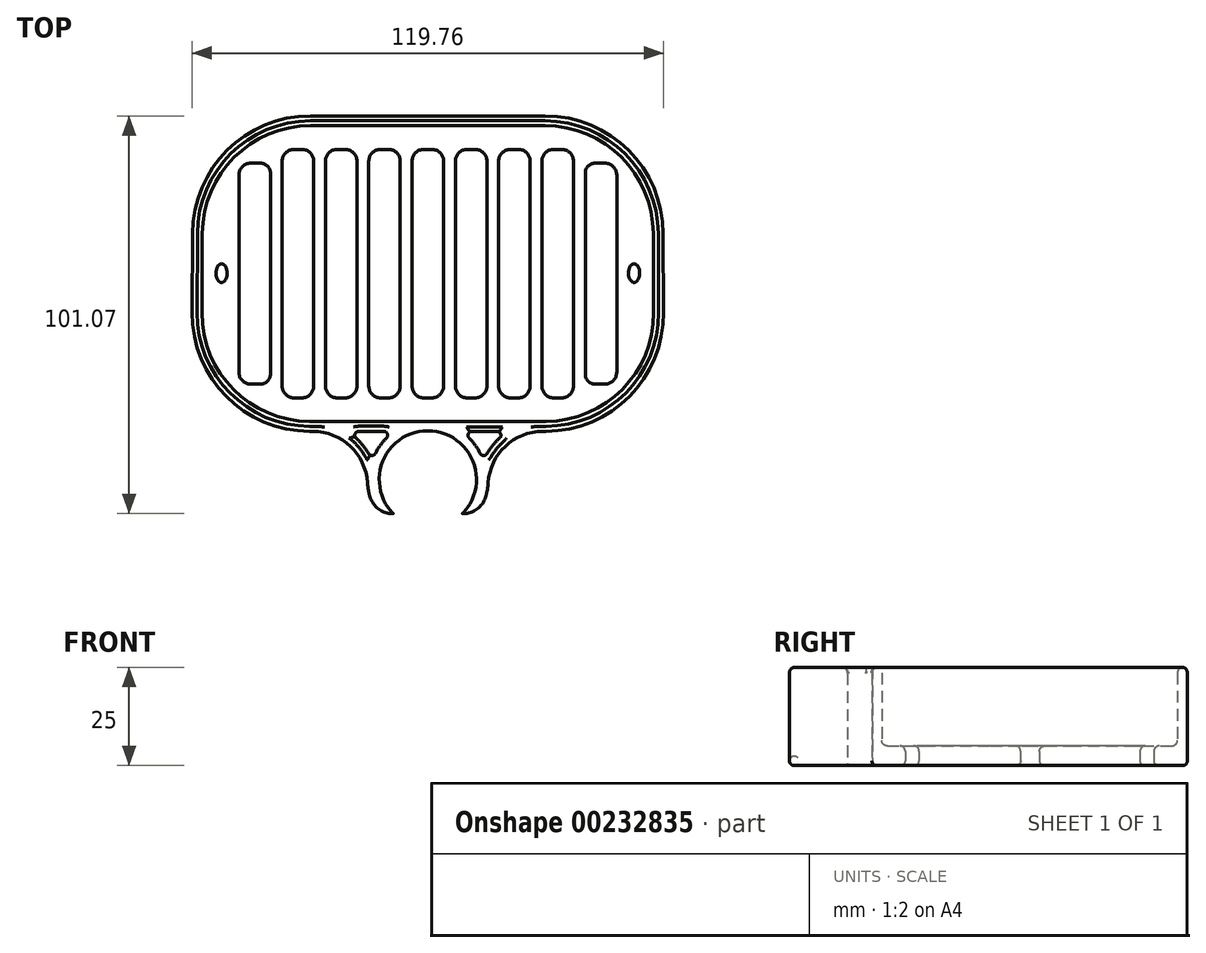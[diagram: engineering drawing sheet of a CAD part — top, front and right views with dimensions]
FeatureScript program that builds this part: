
annotation { "Feature Type Name" : "Feature", "Feature Type Description" : "" }
export const myFeature = defineFeature(function(context is Context, id is Id, definition is map)
    precondition{}
    {
        {
            var Q0;
            Q0=qCreatedBy(makeId("Top.planeOp"),FACE);
            var sketch = newSketch(context, id + "F0", { "sketchPlane" : qUnion([Q0])});
            skArc(sketch, "E0", {"start": v(8.75, -8.72) * mm, "mid": v(0, 12.35) * mm, "end": v(-8.75, -8.72) * mm});
            skLineSegment(sketch, "E1", {"start": v(8.95, -8.72) * mm, "end": v(8.75, -8.72) * mm});
            skArc(sketch, "E2.0", {"start": v(14.69, -4.46) * mm, "mid": v(15.1, -2.71) * mm, "end": v(15.32, -0.93) * mm});
            skLineSegment(sketch, "E3.trimOffspring", {"start": v(-8.75, -8.72) * mm, "end": v(-8.95, -8.72) * mm});
            skArc(sketch, "E4.trimOffspring", {"start": v(-15.32, -0.93) * mm, "mid": v(-15.1, -2.71) * mm, "end": v(-14.69, -4.46) * mm});
            skPoint(sketch, "E5.visualSharp", {"position": v(-12.64, -8.72) * mm});
            skArc(sketch, "E5.filletArc", {"start": v(-14.69, -4.46) * mm, "mid": v(-12.52, -7.53) * mm, "end": v(-8.95, -8.72) * mm});
            skPoint(sketch, "E6.visualSharp", {"position": v(12.64, -8.72) * mm});
            skArc(sketch, "E6.filletArc", {"start": v(8.95, -8.72) * mm, "mid": v(12.52, -7.53) * mm, "end": v(14.69, -4.46) * mm});
            skLineSegment(sketch, "E7", {"start": v(-30, 12.23) * mm, "end": v(-29.24, 12.22) * mm});
            skPoint(sketch, "E7.startSnap0", {"position": v(0, 12.35) * mm});
            skLineSegment(sketch, "E8", {"start": v(-59.88, 42.35) * mm, "end": v(-59.8, 62.47) * mm});
            skLineSegment(sketch, "E9", {"start": v(-29.8, 92.35) * mm, "end": v(0, 92.35) * mm});
            skLineSegment(sketch, "E10.MirrorCS", {"start": v(29.8, 92.35) * mm, "end": v(0, 92.35) * mm});
            skLineSegment(sketch, "E11.MirrorCS", {"start": v(59.88, 42.35) * mm, "end": v(59.8, 62.47) * mm});
            skLineSegment(sketch, "E12.MirrorCS", {"start": v(30, 12.23) * mm, "end": v(29.24, 12.22) * mm});
            skArc(sketch, "E13.filletArc", {"start": v(29.24, 12.22) * mm, "mid": v(19.68, 8.4) * mm, "end": v(15.32, -0.93) * mm});
            skArc(sketch, "E14.filletArc", {"start": v(-15.32, -0.93) * mm, "mid": v(-19.68, 8.4) * mm, "end": v(-29.24, 12.22) * mm});
            skPoint(sketch, "E15.visualSharp", {"position": v(-59.67, 92.35) * mm});
            skArc(sketch, "E15.filletArc", {"start": v(-29.8, 92.35) * mm, "mid": v(-50.96, 83.6) * mm, "end": v(-59.8, 62.47) * mm});
            skPoint(sketch, "E16.visualSharp", {"position": v(59.67, 92.35) * mm});
            skArc(sketch, "E16.filletArc", {"start": v(59.8, 62.47) * mm, "mid": v(50.96, 83.6) * mm, "end": v(29.8, 92.35) * mm});
            skPoint(sketch, "E17.visualSharp", {"position": v(60, 12.35) * mm});
            skArc(sketch, "E17.filletArc", {"start": v(30, 12.23) * mm, "mid": v(51.18, 21.1) * mm, "end": v(59.88, 42.35) * mm});
            skPoint(sketch, "E18.visualSharp", {"position": v(-60, 12.35) * mm});
            skArc(sketch, "E18.filletArc", {"start": v(-59.88, 42.35) * mm, "mid": v(-51.18, 21.1) * mm, "end": v(-30, 12.23) * mm});
            skLineSegment(sketch, "E19.0", {"start": v(29.99, 14.73) * mm, "end": v(25.24, 14.7) * mm});
            skArc(sketch, "E19.1", {"start": v(29.99, 14.73) * mm, "mid": v(49.4, 22.86) * mm, "end": v(57.38, 42.34) * mm});
            skLineSegment(sketch, "E19.2", {"start": v(57.38, 42.34) * mm, "end": v(57.3, 62.46) * mm});
            skArc(sketch, "E19.3", {"start": v(57.3, 62.46) * mm, "mid": v(49.2, 81.83) * mm, "end": v(29.8, 89.85) * mm});
            skLineSegment(sketch, "E19.4", {"start": v(29.8, 89.85) * mm, "end": v(0, 89.85) * mm});
            skLineSegment(sketch, "E19.5", {"start": v(-29.8, 89.85) * mm, "end": v(0, 89.85) * mm});
            skLineSegment(sketch, "E19.6", {"start": v(-29.99, 14.73) * mm, "end": v(-25.24, 14.7) * mm});
            skArc(sketch, "E19.7", {"start": v(-57.38, 42.34) * mm, "mid": v(-49.4, 22.86) * mm, "end": v(-29.99, 14.73) * mm});
            skLineSegment(sketch, "E19.8", {"start": v(-57.38, 42.34) * mm, "end": v(-57.3, 62.46) * mm});
            skArc(sketch, "E19.9", {"start": v(-29.8, 89.85) * mm, "mid": v(-49.2, 81.83) * mm, "end": v(-57.3, 62.46) * mm});
            skLineSegment(sketch, "E20", {"start": v(-25.24, 14.7) * mm, "end": v(25.24, 14.7) * mm});
            skLineSegment(sketch, "E21.bottom", {"start": v(-1, 83.85) * mm, "end": v(1, 83.85) * mm});
            skLineSegment(sketch, "E21.top", {"start": v(-1, 20.7) * mm, "end": v(1, 20.7) * mm});
            skLineSegment(sketch, "E21.left", {"start": v(-4, 80.85) * mm, "end": v(-4, 23.7) * mm});
            skLineSegment(sketch, "E21.right", {"start": v(4, 80.85) * mm, "end": v(4, 23.7) * mm});
            skPoint(sketch, "E22.visualSharp", {"position": v(-4, 83.85) * mm});
            skArc(sketch, "E22.filletArc", {"start": v(-1, 83.85) * mm, "mid": v(-3.12, 82.97) * mm, "end": v(-4, 80.85) * mm});
            skPoint(sketch, "E23.visualSharp", {"position": v(-4, 20.7) * mm});
            skArc(sketch, "E23.filletArc", {"start": v(-4, 23.7) * mm, "mid": v(-3.12, 21.59) * mm, "end": v(-1, 20.7) * mm});
            skPoint(sketch, "E24.visualSharp", {"position": v(4, 20.7) * mm});
            skArc(sketch, "E24.filletArc", {"start": v(1, 20.7) * mm, "mid": v(3.12, 21.59) * mm, "end": v(4, 23.7) * mm});
            skPoint(sketch, "E25.visualSharp", {"position": v(4, 83.85) * mm});
            skArc(sketch, "E25.filletArc", {"start": v(4, 80.85) * mm, "mid": v(3.12, 82.97) * mm, "end": v(1, 83.85) * mm});
            skPoint(sketch, "E26.1.0.0", {"position": v(7, 20.7) * mm});
            skLineSegment(sketch, "E26.1.0.1", {"start": v(7, 80.85) * mm, "end": v(7, 23.7) * mm});
            skPoint(sketch, "E26.1.0.2", {"position": v(7, 83.85) * mm});
            skPoint(sketch, "E26.1.0.3", {"position": v(15, 83.85) * mm});
            skPoint(sketch, "E26.1.0.4", {"position": v(15, 20.7) * mm});
            skLineSegment(sketch, "E26.1.0.5", {"start": v(15, 80.85) * mm, "end": v(15, 23.7) * mm});
            skArc(sketch, "E26.1.0.6", {"start": v(12, 20.7) * mm, "mid": v(14.12, 21.59) * mm, "end": v(15, 23.7) * mm});
            skArc(sketch, "E26.1.0.7", {"start": v(15, 80.85) * mm, "mid": v(14.12, 82.97) * mm, "end": v(12, 83.85) * mm});
            skArc(sketch, "E26.1.0.8", {"start": v(10, 83.85) * mm, "mid": v(7.88, 82.97) * mm, "end": v(7, 80.85) * mm});
            skLineSegment(sketch, "E26.1.0.9", {"start": v(10, 20.7) * mm, "end": v(12, 20.7) * mm});
            skArc(sketch, "E26.1.0.10", {"start": v(7, 23.7) * mm, "mid": v(7.88, 21.59) * mm, "end": v(10, 20.7) * mm});
            skLineSegment(sketch, "E26.1.0.11", {"start": v(10, 83.85) * mm, "end": v(12, 83.85) * mm});
            skPoint(sketch, "E26.2.0.0", {"position": v(18, 20.7) * mm});
            skLineSegment(sketch, "E26.2.0.1", {"start": v(18, 80.85) * mm, "end": v(18, 23.7) * mm});
            skPoint(sketch, "E26.2.0.2", {"position": v(18, 83.85) * mm});
            skPoint(sketch, "E26.2.0.3", {"position": v(26, 83.85) * mm});
            skPoint(sketch, "E26.2.0.4", {"position": v(26, 20.7) * mm});
            skLineSegment(sketch, "E26.2.0.5", {"start": v(26, 80.85) * mm, "end": v(26, 23.7) * mm});
            skArc(sketch, "E26.2.0.6", {"start": v(23, 20.7) * mm, "mid": v(25.12, 21.59) * mm, "end": v(26, 23.7) * mm});
            skArc(sketch, "E26.2.0.7", {"start": v(26, 80.85) * mm, "mid": v(25.12, 82.97) * mm, "end": v(23, 83.85) * mm});
            skArc(sketch, "E26.2.0.8", {"start": v(21, 83.85) * mm, "mid": v(18.88, 82.97) * mm, "end": v(18, 80.85) * mm});
            skLineSegment(sketch, "E26.2.0.9", {"start": v(21, 20.7) * mm, "end": v(23, 20.7) * mm});
            skArc(sketch, "E26.2.0.10", {"start": v(18, 23.7) * mm, "mid": v(18.88, 21.59) * mm, "end": v(21, 20.7) * mm});
            skLineSegment(sketch, "E26.2.0.11", {"start": v(21, 83.85) * mm, "end": v(23, 83.85) * mm});
            skPoint(sketch, "E26.3.0.0", {"position": v(29, 20.7) * mm});
            skLineSegment(sketch, "E26.3.0.1", {"start": v(29, 80.85) * mm, "end": v(29, 23.7) * mm});
            skPoint(sketch, "E26.3.0.2", {"position": v(29, 83.85) * mm});
            skPoint(sketch, "E26.3.0.3", {"position": v(37, 83.85) * mm});
            skPoint(sketch, "E26.3.0.4", {"position": v(37, 20.7) * mm});
            skLineSegment(sketch, "E26.3.0.5", {"start": v(37, 80.85) * mm, "end": v(37, 23.7) * mm});
            skArc(sketch, "E26.3.0.6", {"start": v(34, 20.7) * mm, "mid": v(36.12, 21.59) * mm, "end": v(37, 23.7) * mm});
            skArc(sketch, "E26.3.0.7", {"start": v(37, 80.85) * mm, "mid": v(36.12, 82.97) * mm, "end": v(34, 83.85) * mm});
            skArc(sketch, "E26.3.0.8", {"start": v(32, 83.85) * mm, "mid": v(29.88, 82.97) * mm, "end": v(29, 80.85) * mm});
            skLineSegment(sketch, "E26.3.0.9", {"start": v(32, 20.7) * mm, "end": v(34, 20.7) * mm});
            skArc(sketch, "E26.3.0.10", {"start": v(29, 23.7) * mm, "mid": v(29.88, 21.59) * mm, "end": v(32, 20.7) * mm});
            skLineSegment(sketch, "E26.3.0.11", {"start": v(32, 83.85) * mm, "end": v(34, 83.85) * mm});
            skPoint(sketch, "E26.4.0.0", {"position": v(40, 20.7) * mm});
            skLineSegment(sketch, "E26.4.0.1", {"start": v(40, 77.85) * mm, "end": v(40, 26.7) * mm});
            skPoint(sketch, "E26.4.0.2", {"position": v(40, 83.85) * mm});
            skPoint(sketch, "E26.4.0.3", {"position": v(48, 83.85) * mm});
            skPoint(sketch, "E26.4.0.4", {"position": v(48, 20.7) * mm});
            skLineSegment(sketch, "E26.4.0.5", {"start": v(48, 77.34) * mm, "end": v(48, 27.22) * mm});
            skLineSegment(sketch, "E26.direction1", {"start": v(-4, 20.7) * mm, "end": v(7, 20.7) * mm, "construction": true});
            skPoint(sketch, "E27.centerSnap0", {"position": v(4, 52.28) * mm});
            skEllipse(sketch, "E28", {"center": v(52.4, 52.4) * mm, "majorRadius": 2.38 * mm, "minorRadius": 1.43 * mm, "majorAxis": v(0, 1)});
            skPoint(sketch, "E28.centerSnap0", {"position": v(48, 52.4) * mm});
            skLineSegment(sketch, "E29.MirrorCS", {"start": v(-10, 20.7) * mm, "end": v(-12, 20.7) * mm});
            skArc(sketch, "E30.MirrorCS", {"start": v(-21, 83.85) * mm, "mid": v(-18.88, 82.97) * mm, "end": v(-18, 80.85) * mm});
            skLineSegment(sketch, "E31.MirrorCS", {"start": v(-10, 83.85) * mm, "end": v(-12, 83.85) * mm});
            skLineSegment(sketch, "E32.MirrorCS", {"start": v(-32, 83.85) * mm, "end": v(-34, 83.85) * mm});
            skLineSegment(sketch, "E33.MirrorCS", {"start": v(-32, 20.7) * mm, "end": v(-34, 20.7) * mm});
            skLineSegment(sketch, "E34.MirrorCS", {"start": v(-21, 20.7) * mm, "end": v(-23, 20.7) * mm});
            skArc(sketch, "E35.MirrorCS", {"start": v(-32, 83.85) * mm, "mid": v(-29.88, 82.97) * mm, "end": v(-29, 80.85) * mm});
            skArc(sketch, "E36.MirrorCS", {"start": v(-7, 23.7) * mm, "mid": v(-7.88, 21.59) * mm, "end": v(-10, 20.7) * mm});
            skArc(sketch, "E37.MirrorCS", {"start": v(-37, 80.85) * mm, "mid": v(-36.12, 82.97) * mm, "end": v(-34, 83.85) * mm});
            skArc(sketch, "E38.MirrorCS", {"start": v(-26, 80.85) * mm, "mid": v(-25.12, 82.97) * mm, "end": v(-23, 83.85) * mm});
            skLineSegment(sketch, "E39.MirrorCS", {"start": v(-21, 83.85) * mm, "end": v(-23, 83.85) * mm});
            skArc(sketch, "E40.MirrorCS", {"start": v(-15, 80.85) * mm, "mid": v(-14.12, 82.97) * mm, "end": v(-12, 83.85) * mm});
            skArc(sketch, "E41.MirrorCS", {"start": v(-18, 23.7) * mm, "mid": v(-18.88, 21.59) * mm, "end": v(-21, 20.7) * mm});
            skArc(sketch, "E42.MirrorCS", {"start": v(-10, 83.85) * mm, "mid": v(-7.88, 82.97) * mm, "end": v(-7, 80.85) * mm});
            skArc(sketch, "E43.MirrorCS", {"start": v(-23, 20.7) * mm, "mid": v(-25.12, 21.59) * mm, "end": v(-26, 23.7) * mm});
            skArc(sketch, "E44.MirrorCS", {"start": v(-29, 23.7) * mm, "mid": v(-29.88, 21.59) * mm, "end": v(-32, 20.7) * mm});
            skArc(sketch, "E45.MirrorCS", {"start": v(-12, 20.7) * mm, "mid": v(-14.12, 21.59) * mm, "end": v(-15, 23.7) * mm});
            skArc(sketch, "E46.MirrorCS", {"start": v(-34, 20.7) * mm, "mid": v(-36.12, 21.59) * mm, "end": v(-37, 23.7) * mm});
            skPoint(sketch, "E47.MirrorP", {"position": v(-26, 20.7) * mm});
            skPoint(sketch, "E48.MirrorP", {"position": v(-48, 20.7) * mm});
            skPoint(sketch, "E49.MirrorP", {"position": v(-26, 83.85) * mm});
            skPoint(sketch, "E50.MirrorP", {"position": v(-18, 20.7) * mm});
            skPoint(sketch, "E51.MirrorP", {"position": v(-48, 83.85) * mm});
            skPoint(sketch, "E52.MirrorP", {"position": v(-29, 83.85) * mm});
            skLineSegment(sketch, "E53.MirrorCS", {"start": v(-48, 77.34) * mm, "end": v(-48, 27.22) * mm});
            skPoint(sketch, "E54.MirrorP", {"position": v(-40, 20.7) * mm});
            skLineSegment(sketch, "E55.MirrorCS", {"start": v(-26, 80.85) * mm, "end": v(-26, 23.7) * mm});
            skPoint(sketch, "E56.MirrorP", {"position": v(-18, 83.85) * mm});
            skPoint(sketch, "E57.MirrorP", {"position": v(-37, 20.7) * mm});
            skPoint(sketch, "E58.MirrorP", {"position": v(-15, 20.7) * mm});
            skLineSegment(sketch, "E59.MirrorCS", {"start": v(-15, 80.85) * mm, "end": v(-15, 23.7) * mm});
            skPoint(sketch, "E60.MirrorP", {"position": v(-7, 20.7) * mm});
            skPoint(sketch, "E61.MirrorP", {"position": v(-29, 20.7) * mm});
            skPoint(sketch, "E62.MirrorP", {"position": v(-15, 83.85) * mm});
            skPoint(sketch, "E63.MirrorP", {"position": v(-48, 52.4) * mm});
            skLineSegment(sketch, "E64.MirrorCS", {"start": v(-40, 77.85) * mm, "end": v(-40, 26.7) * mm});
            skPoint(sketch, "E65.MirrorP", {"position": v(-7, 83.85) * mm});
            skPoint(sketch, "E66.MirrorP", {"position": v(-4, 52.28) * mm});
            skLineSegment(sketch, "E67.MirrorCS", {"start": v(-29, 80.85) * mm, "end": v(-29, 23.7) * mm});
            skEllipse(sketch, "E68.MirrorC", {"center": v(-52.4, 52.4) * mm, "majorRadius": 2.38 * mm, "minorRadius": 1.43 * mm, "majorAxis": v(0, 1)});
            skPoint(sketch, "E69.MirrorP", {"position": v(-37, 83.85) * mm});
            skLineSegment(sketch, "E70.MirrorCS", {"start": v(-18, 80.85) * mm, "end": v(-18, 23.7) * mm});
            skLineSegment(sketch, "E71.MirrorCS", {"start": v(-7, 80.85) * mm, "end": v(-7, 23.7) * mm});
            skPoint(sketch, "E72.MirrorP", {"position": v(-40, 83.85) * mm});
            skLineSegment(sketch, "E73.MirrorCS", {"start": v(-37, 80.85) * mm, "end": v(-37, 23.7) * mm});
            skLineSegment(sketch, "E74", {"start": v(42.49, 80.34) * mm, "end": v(45, 80.34) * mm});
            skPoint(sketch, "E26.4.0.11.start.orphan", {"position": v(43, 84.35) * mm});
            skPoint(sketch, "E26.4.0.7.end.orphan", {"position": v(45, 84.35) * mm});
            skPoint(sketch, "E75.newPointA", {"position": v(40, 80.85) * mm});
            skArc(sketch, "E75.filletArc", {"start": v(42.49, 80.34) * mm, "mid": v(40.73, 79.6) * mm, "end": v(40, 77.85) * mm});
            skPoint(sketch, "E76.newPointB", {"position": v(48, 80.85) * mm});
            skArc(sketch, "E76.filletArc", {"start": v(48, 77.34) * mm, "mid": v(47.12, 79.46) * mm, "end": v(45, 80.34) * mm});
            skLineSegment(sketch, "E77", {"start": v(4, 52.28) * mm, "end": v(-4, 52.28) * mm, "construction": true});
            skLineSegment(sketch, "E78.MirrorCS", {"start": v(42.49, 24.22) * mm, "end": v(45, 24.22) * mm});
            skArc(sketch, "E79.MirrorCS", {"start": v(42.49, 24.22) * mm, "mid": v(40.73, 24.95) * mm, "end": v(40, 26.7) * mm});
            skArc(sketch, "E80.MirrorCS", {"start": v(48, 27.22) * mm, "mid": v(47.12, 25.1) * mm, "end": v(45, 24.22) * mm});
            skPoint(sketch, "E26.4.0.6.end.orphan", {"position": v(48, 23.96) * mm});
            skPoint(sketch, "E26.4.0.9.end.orphan", {"position": v(45, 20.35) * mm});
            skPoint(sketch, "E26.4.0.10.end.orphan", {"position": v(43, 20.35) * mm});
            skPoint(sketch, "E81.orphan", {"position": v(40, 23.7) * mm});
            skArc(sketch, "E82.MirrorCS", {"start": v(-48, 27.22) * mm, "mid": v(-47.12, 25.1) * mm, "end": v(-45, 24.22) * mm});
            skLineSegment(sketch, "E83.MirrorCS", {"start": v(-42.49, 24.22) * mm, "end": v(-45, 24.22) * mm});
            skArc(sketch, "E84.MirrorCS", {"start": v(-42.49, 24.22) * mm, "mid": v(-40.73, 24.95) * mm, "end": v(-40, 26.7) * mm});
            skArc(sketch, "E85.MirrorCS", {"start": v(-42.49, 80.34) * mm, "mid": v(-40.73, 79.6) * mm, "end": v(-40, 77.85) * mm});
            skLineSegment(sketch, "E86.MirrorCS", {"start": v(-42.49, 80.34) * mm, "end": v(-45, 80.34) * mm});
            skArc(sketch, "E87.MirrorCS", {"start": v(-48, 77.34) * mm, "mid": v(-47.12, 79.46) * mm, "end": v(-45, 80.34) * mm});
            skPoint(sketch, "E88.MirrorCS.start.orphan", {"position": v(-43, 84.35) * mm});
            skPoint(sketch, "E89.orphan", {"position": v(-40, 80.85) * mm});
            skPoint(sketch, "E90.MirrorCS.end.orphan", {"position": v(-45, 84.35) * mm});
            skPoint(sketch, "E90.MirrorCS.start.orphan", {"position": v(-48, 80.85) * mm});
            skPoint(sketch, "E91.MirrorCS.start.orphan", {"position": v(-43, 20.35) * mm});
            skPoint(sketch, "E92.MirrorCS.start.orphan", {"position": v(-45, 20.35) * mm});
            skPoint(sketch, "E93.orphan", {"position": v(-48, 23.96) * mm});
            skPoint(sketch, "E94.orphan", {"position": v(-40, 23.7) * mm});
            skLineSegment(sketch, "E95", {"start": v(0, 0) * mm, "end": v(-20.84, -20.84) * mm});
            skArc(sketch, "E96.0", {"start": v(18.23, 10.46) * mm, "mid": v(16.5, 8.63) * mm, "end": v(15.05, 6.55) * mm});
            skLineSegment(sketch, "E97.trimOffspring", {"start": v(11.2, 12.2) * mm, "end": v(17.56, 12.2) * mm});
            skArc(sketch, "E98.trimOffspring", {"start": v(13.3, 6.61) * mm, "mid": v(12.06, 8.67) * mm, "end": v(10.5, 10.5) * mm});
            skPoint(sketch, "E99.visualSharp", {"position": v(20.54, 12.2) * mm});
            skArc(sketch, "E99.filletArc", {"start": v(18.23, 10.46) * mm, "mid": v(18.5, 11.57) * mm, "end": v(17.56, 12.2) * mm});
            skPoint(sketch, "E100.visualSharp", {"position": v(8.46, 12.2) * mm});
            skArc(sketch, "E100.filletArc", {"start": v(11.2, 12.2) * mm, "mid": v(10.28, 11.59) * mm, "end": v(10.5, 10.5) * mm});
            skPoint(sketch, "E101.visualSharp", {"position": v(14.1, 4.66) * mm});
            skArc(sketch, "E101.filletArc", {"start": v(13.3, 6.61) * mm, "mid": v(14.16, 6.06) * mm, "end": v(15.05, 6.55) * mm});
            skArc(sketch, "E102.MirrorCS", {"start": v(-11.2, 12.2) * mm, "mid": v(-10.28, 11.59) * mm, "end": v(-10.5, 10.5) * mm});
            skArc(sketch, "E103.MirrorCS", {"start": v(-13.3, 6.61) * mm, "mid": v(-14.16, 6.06) * mm, "end": v(-15.05, 6.55) * mm});
            skArc(sketch, "E104.MirrorCS", {"start": v(-18.23, 10.46) * mm, "mid": v(-18.5, 11.57) * mm, "end": v(-17.56, 12.2) * mm});
            skArc(sketch, "E105.MirrorCS", {"start": v(-13.3, 6.61) * mm, "mid": v(-12.06, 8.67) * mm, "end": v(-10.5, 10.5) * mm});
            skLineSegment(sketch, "E106.MirrorCS", {"start": v(-11.2, 12.2) * mm, "end": v(-17.56, 12.2) * mm});
            skArc(sketch, "E107.MirrorCS", {"start": v(-18.23, 10.46) * mm, "mid": v(-16.5, 8.63) * mm, "end": v(-15.05, 6.55) * mm});
            skSolve(sketch);
        }
        {
            var Q0;
            Q0=makeQuery(id+"F0.imprint","IMPRINT",FACE,{"disambiguationData":[TD([[makeQuery(id+"F0.imprint","IMPRINT",EDGE,{"derivedFrom":sQuery(id+"F0.wireOp",EDGE,"E0")}),-1.0]])]});
            extrude(context, id + "F1", {"entities" : qUnion([Q0]), "depth" : 25 * mm});
        }
        {
            var Q0;
            Q0=makeQuery(id+"F0.imprint","IMPRINT",FACE,{"disambiguationData":[TD([[makeQuery(id+"F0.imprint","IMPRINT",EDGE,{"derivedFrom":sQuery(id+"F0.wireOp",EDGE,"E19.0")}),-1.0]])]});
            extrude(context, id + "F2", {"entities" : qUnion([Q0]), "operationType" : NewBodyOperationType.ADD, "depth" : 5 * mm});
        }
        {
            var Q0;
            Q0=makeQuery(id+"F2.opExtrude","CAP_FACE",FACE,{"disambiguationData":[OSD([sQuery(id+"F0.wireOp",EDGE,"E19.0"),sQuery(id+"F0.wireOp",EDGE,"E19.1"),sQuery(id+"F0.wireOp",EDGE,"E19.2"),sQuery(id+"F0.wireOp",EDGE,"E19.3"),sQuery(id+"F0.wireOp",EDGE,"E19.4"),sQuery(id+"F0.wireOp",EDGE,"E19.5"),sQuery(id+"F0.wireOp",EDGE,"E19.6"),sQuery(id+"F0.wireOp",EDGE,"E19.7"),sQuery(id+"F0.wireOp",EDGE,"E19.9"),sQuery(id+"F0.wireOp",EDGE,"E20"),sQuery(id+"F0.wireOp",EDGE,"E21.bottom"),sQuery(id+"F0.wireOp",EDGE,"E21.top"),sQuery(id+"F0.wireOp",EDGE,"E21.left"),sQuery(id+"F0.wireOp",EDGE,"E21.right"),sQuery(id+"F0.wireOp",EDGE,"E22.filletArc"),sQuery(id+"F0.wireOp",EDGE,"E23.filletArc"),sQuery(id+"F0.wireOp",EDGE,"E24.filletArc"),sQuery(id+"F0.wireOp",EDGE,"E25.filletArc"),sQuery(id+"F0.wireOp",EDGE,"E26.1.0.1"),sQuery(id+"F0.wireOp",EDGE,"E26.1.0.5"),sQuery(id+"F0.wireOp",EDGE,"E26.1.0.6"),sQuery(id+"F0.wireOp",EDGE,"E26.1.0.7"),sQuery(id+"F0.wireOp",EDGE,"E26.1.0.8"),sQuery(id+"F0.wireOp",EDGE,"E26.1.0.9"),sQuery(id+"F0.wireOp",EDGE,"E26.1.0.10"),sQuery(id+"F0.wireOp",EDGE,"E26.1.0.11"),sQuery(id+"F0.wireOp",EDGE,"E26.2.0.1"),sQuery(id+"F0.wireOp",EDGE,"E26.2.0.5"),sQuery(id+"F0.wireOp",EDGE,"E26.2.0.6"),sQuery(id+"F0.wireOp",EDGE,"E26.2.0.7"),sQuery(id+"F0.wireOp",EDGE,"E26.2.0.8"),sQuery(id+"F0.wireOp",EDGE,"E26.2.0.9"),sQuery(id+"F0.wireOp",EDGE,"E26.2.0.10"),sQuery(id+"F0.wireOp",EDGE,"E26.2.0.11"),sQuery(id+"F0.wireOp",EDGE,"E26.3.0.1"),sQuery(id+"F0.wireOp",EDGE,"E26.3.0.5"),sQuery(id+"F0.wireOp",EDGE,"E26.3.0.6"),sQuery(id+"F0.wireOp",EDGE,"E26.3.0.7"),sQuery(id+"F0.wireOp",EDGE,"E26.3.0.8"),sQuery(id+"F0.wireOp",EDGE,"E26.3.0.9"),sQuery(id+"F0.wireOp",EDGE,"E26.3.0.10"),sQuery(id+"F0.wireOp",EDGE,"E26.3.0.11"),sQuery(id+"F0.wireOp",EDGE,"E26.4.0.1"),sQuery(id+"F0.wireOp",EDGE,"E26.4.0.5"),sQuery(id+"F0.wireOp",EDGE,"E26.4.0.6"),sQuery(id+"F0.wireOp",EDGE,"E26.4.0.7"),sQuery(id+"F0.wireOp",EDGE,"E26.4.0.8"),sQuery(id+"F0.wireOp",EDGE,"E26.4.0.9"),sQuery(id+"F0.wireOp",EDGE,"E26.4.0.10"),sQuery(id+"F0.wireOp",EDGE,"E26.4.0.11"),sQuery(id+"F0.wireOp",EDGE,"E28"),sQuery(id+"F0.wireOp",EDGE,"E29.MirrorCS"),sQuery(id+"F0.wireOp",EDGE,"E30.MirrorCS"),sQuery(id+"F0.wireOp",EDGE,"E31.MirrorCS"),sQuery(id+"F0.wireOp",EDGE,"E32.MirrorCS"),sQuery(id+"F0.wireOp",EDGE,"E33.MirrorCS"),sQuery(id+"F0.wireOp",EDGE,"E34.MirrorCS"),sQuery(id+"F0.wireOp",EDGE,"E91.MirrorCS"),sQuery(id+"F0.wireOp",EDGE,"E35.MirrorCS"),sQuery(id+"F0.wireOp",EDGE,"E36.MirrorCS"),sQuery(id+"F0.wireOp",EDGE,"E37.MirrorCS"),sQuery(id+"F0.wireOp",EDGE,"E92.MirrorCS"),sQuery(id+"F0.wireOp",EDGE,"E38.MirrorCS"),sQuery(id+"F0.wireOp",EDGE,"E39.MirrorCS"),sQuery(id+"F0.wireOp",EDGE,"E40.MirrorCS"),sQuery(id+"F0.wireOp",EDGE,"E304.MirrorCS"),sQuery(id+"F0.wireOp",EDGE,"E90.MirrorCS"),sQuery(id+"F0.wireOp",EDGE,"E88.MirrorCS"),sQuery(id+"F0.wireOp",EDGE,"E41.MirrorCS"),sQuery(id+"F0.wireOp",EDGE,"E308.MirrorCS"),sQuery(id+"F0.wireOp",EDGE,"E42.MirrorCS"),sQuery(id+"F0.wireOp",EDGE,"E43.MirrorCS"),sQuery(id+"F0.wireOp",EDGE,"E44.MirrorCS"),sQuery(id+"F0.wireOp",EDGE,"E45.MirrorCS"),sQuery(id+"F0.wireOp",EDGE,"E46.MirrorCS"),sQuery(id+"F0.wireOp",EDGE,"E53.MirrorCS"),sQuery(id+"F0.wireOp",EDGE,"E55.MirrorCS"),sQuery(id+"F0.wireOp",EDGE,"E19.8"),sQuery(id+"F0.wireOp",EDGE,"E59.MirrorCS"),sQuery(id+"F0.wireOp",EDGE,"E64.MirrorCS"),sQuery(id+"F0.wireOp",EDGE,"E67.MirrorCS"),sQuery(id+"F0.wireOp",EDGE,"E68.MirrorC"),sQuery(id+"F0.wireOp",EDGE,"E70.MirrorCS"),sQuery(id+"F0.wireOp",EDGE,"E71.MirrorCS"),sQuery(id+"F0.wireOp",EDGE,"E73.MirrorCS")])],"isStart":false});
            var Q1;
            Q1=makeQuery(id+"F1.opExtrude","CAP_EDGE",EDGE,{"disambiguationData":[OSD([sQuery(id+"F0.wireOp",EDGE,"E9"),sQuery(id+"F0.wireOp",EDGE,"E10.MirrorCS")])],"isStart":false});
            var Q2;
            Q2=makeQuery(id+"F1.opExtrude","CAP_EDGE",EDGE,{"disambiguationData":[OSD([sQuery(id+"F0.wireOp",EDGE,"E16.filletArc")])],"isStart":false});
            var Q3;
            Q3=makeQuery(id+"F1.opExtrude","CAP_EDGE",EDGE,{"disambiguationData":[OSD([sQuery(id+"F0.wireOp",EDGE,"E11.MirrorCS")])],"isStart":false});
            var Q4;
            Q4=makeQuery(id+"F1.opExtrude","CAP_EDGE",EDGE,{"disambiguationData":[OSD([sQuery(id+"F0.wireOp",EDGE,"E17.filletArc")])],"isStart":false});
            var Q5;
            Q5=makeQuery(id+"F1.opExtrude","CAP_EDGE",EDGE,{"disambiguationData":[OSD([sQuery(id+"F0.wireOp",EDGE,"E19.0"),sQuery(id+"F0.wireOp",EDGE,"E19.6"),sQuery(id+"F0.wireOp",EDGE,"E20")])],"isStart":false});
            fillet(context, id + "F3", {"entities" : qUnion([Q0, Q1, Q2, Q3, Q4, Q5]), "radius" : 1.4 * mm, "tangentPropagation" : true, "allowEdgeOverflow" : false});
        }
        {
            var Q0;
            Q0=makeQuery(id+"F1.opExtrude","CAP_EDGE",EDGE,{"disambiguationData":[OSD([sQuery(id+"F0.wireOp",EDGE,"E6.filletArc")])],"isStart":true});
            var Q1;
            Q1=makeQuery(id+"F1.opExtrude","CAP_EDGE",EDGE,{"disambiguationData":[OSD([sQuery(id+"F0.wireOp",EDGE,"E2.0")])],"isStart":true});
            var Q2;
            Q2=makeQuery(id+"F1.opExtrude","CAP_EDGE",EDGE,{"disambiguationData":[OSD([sQuery(id+"F0.wireOp",EDGE,"E13.filletArc")])],"isStart":true});
            var Q3;
            Q3=makeQuery(id+"F1.opExtrude","CAP_EDGE",EDGE,{"disambiguationData":[OSD([sQuery(id+"F0.wireOp",EDGE,"E5.filletArc")])],"isStart":true});
            var Q4;
            Q4=makeQuery(id+"F1.opExtrude","CAP_EDGE",EDGE,{"disambiguationData":[OSD([sQuery(id+"F0.wireOp",EDGE,"E4.trimOffspring")])],"isStart":true});
            var Q5;
            Q5=makeQuery(id+"F1.opExtrude","CAP_EDGE",EDGE,{"disambiguationData":[OSD([sQuery(id+"F0.wireOp",EDGE,"E14.filletArc")])],"isStart":true});
            var Q6;
            Q6=makeQuery(id+"F1.opExtrude","CAP_EDGE",EDGE,{"disambiguationData":[OSD([sQuery(id+"F0.wireOp",EDGE,"E18.filletArc")])],"isStart":true});
            var Q7;
            Q7=makeQuery(id+"F1.opExtrude","CAP_EDGE",EDGE,{"disambiguationData":[OSD([sQuery(id+"F0.wireOp",EDGE,"E7")])],"isStart":true});
            var Q8;
            Q8=makeQuery(id+"F1.opExtrude","CAP_EDGE",EDGE,{"disambiguationData":[OSD([sQuery(id+"F0.wireOp",EDGE,"E17.filletArc")])],"isStart":true});
            var Q9;
            Q9=makeQuery(id+"F1.opExtrude","CAP_EDGE",EDGE,{"disambiguationData":[OSD([sQuery(id+"F0.wireOp",EDGE,"E12.MirrorCS")])],"isStart":true});
            var Q10;
            Q10=makeQuery(id+"F1.opExtrude","CAP_EDGE",EDGE,{"disambiguationData":[OSD([sQuery(id+"F0.wireOp",EDGE,"E11.MirrorCS")])],"isStart":true});
            var Q11;
            Q11=makeQuery(id+"F1.opExtrude","CAP_EDGE",EDGE,{"disambiguationData":[OSD([sQuery(id+"F0.wireOp",EDGE,"E16.filletArc")])],"isStart":true});
            var Q12;
            Q12=makeQuery(id+"F1.opExtrude","CAP_EDGE",EDGE,{"disambiguationData":[OSD([sQuery(id+"F0.wireOp",EDGE,"E9"),sQuery(id+"F0.wireOp",EDGE,"E10.MirrorCS")])],"isStart":true});
            var Q13;
            Q13=makeQuery(id+"F1.opExtrude","CAP_EDGE",EDGE,{"disambiguationData":[OSD([sQuery(id+"F0.wireOp",EDGE,"E15.filletArc")])],"isStart":true});
            var Q14;
            Q14=makeQuery(id+"F1.opExtrude","CAP_EDGE",EDGE,{"disambiguationData":[OSD([sQuery(id+"F0.wireOp",EDGE,"E8")])],"isStart":true});
            var Q15;
            Q15=makeQuery(id+"F2.opExtrude","CAP_EDGE",EDGE,{"disambiguationData":[OSD([sQuery(id+"F0.wireOp",EDGE,"E53.MirrorCS")])],"isStart":true});
            var Q16;
            Q16=makeQuery(id+"F2.opExtrude","CAP_EDGE",EDGE,{"disambiguationData":[OSD([sQuery(id+"F0.wireOp",EDGE,"E64.MirrorCS")])],"isStart":true});
            var Q17;
            Q17=makeQuery(id+"F2.opExtrude","CAP_EDGE",EDGE,{"disambiguationData":[OSD([sQuery(id+"F0.wireOp",EDGE,"E67.MirrorCS")])],"isStart":true});
            var Q18;
            Q18=makeQuery(id+"F2.opExtrude","CAP_EDGE",EDGE,{"disambiguationData":[OSD([sQuery(id+"F0.wireOp",EDGE,"E73.MirrorCS")])],"isStart":true});
            var Q19;
            Q19=makeQuery(id+"F2.opExtrude","CAP_EDGE",EDGE,{"disambiguationData":[OSD([sQuery(id+"F0.wireOp",EDGE,"E82.MirrorCS")])],"isStart":true});
            var Q20;
            Q20=makeQuery(id+"F2.opExtrude","CAP_EDGE",EDGE,{"disambiguationData":[OSD([sQuery(id+"F0.wireOp",EDGE,"E55.MirrorCS")])],"isStart":true});
            var Q21;
            Q21=makeQuery(id+"F2.opExtrude","CAP_EDGE",EDGE,{"disambiguationData":[OSD([sQuery(id+"F0.wireOp",EDGE,"E59.MirrorCS")])],"isStart":true});
            var Q22;
            Q22=makeQuery(id+"F2.opExtrude","CAP_EDGE",EDGE,{"disambiguationData":[OSD([sQuery(id+"F0.wireOp",EDGE,"E21.left")])],"isStart":true});
            var Q23;
            Q23=makeQuery(id+"F2.opExtrude","CAP_EDGE",EDGE,{"disambiguationData":[OSD([sQuery(id+"F0.wireOp",EDGE,"E26.1.0.1")])],"isStart":true});
            var Q24;
            Q24=makeQuery(id+"F2.opExtrude","CAP_EDGE",EDGE,{"disambiguationData":[OSD([sQuery(id+"F0.wireOp",EDGE,"E26.2.0.1")])],"isStart":true});
            var Q25;
            Q25=makeQuery(id+"F2.opExtrude","CAP_EDGE",EDGE,{"disambiguationData":[OSD([sQuery(id+"F0.wireOp",EDGE,"E26.3.0.1")])],"isStart":true});
            var Q26;
            Q26=makeQuery(id+"F2.opExtrude","CAP_EDGE",EDGE,{"disambiguationData":[OSD([sQuery(id+"F0.wireOp",EDGE,"E26.4.0.1")])],"isStart":true});
            var Q27;
            Q27=makeQuery(id+"F2.opExtrude","CAP_EDGE",EDGE,{"disambiguationData":[OSD([sQuery(id+"F0.wireOp",EDGE,"E28")])],"isStart":true});
            var Q28;
            Q28=makeQuery(id+"F2.opExtrude","CAP_EDGE",EDGE,{"disambiguationData":[OSD([sQuery(id+"F0.wireOp",EDGE,"E68.MirrorC")])],"isStart":true});
            fillet(context, id + "F4", {"entities" : qUnion([Q0, Q1, Q2, Q3, Q4, Q5, Q6, Q7, Q8, Q9, Q10, Q11, Q12, Q13, Q14, Q15, Q16, Q17, Q18, Q19, Q20, Q21, Q22, Q23, Q24, Q25, Q26, Q27, Q28]), "radius" : 1.2 * mm, "tangentPropagation" : true, "allowEdgeOverflow" : false});
        }
        {
            var Q0;
            Q0=makeQuery(id+"F1.opExtrude","CAP_EDGE",EDGE,{"disambiguationData":[OSD([sQuery(id+"F0.wireOp",EDGE,"E97.trimOffspring")])],"isStart":false});
            var Q1;
            Q1=makeQuery(id+"F1.opExtrude","CAP_EDGE",EDGE,{"disambiguationData":[OSD([sQuery(id+"F0.wireOp",EDGE,"E106.MirrorCS")])],"isStart":false});
            fillet(context, id + "F5", {"entities" : qUnion([Q0, Q1]), "radius" : 1.5 * mm, "tangentPropagation" : true, "allowEdgeOverflow" : false});
        }
    });
